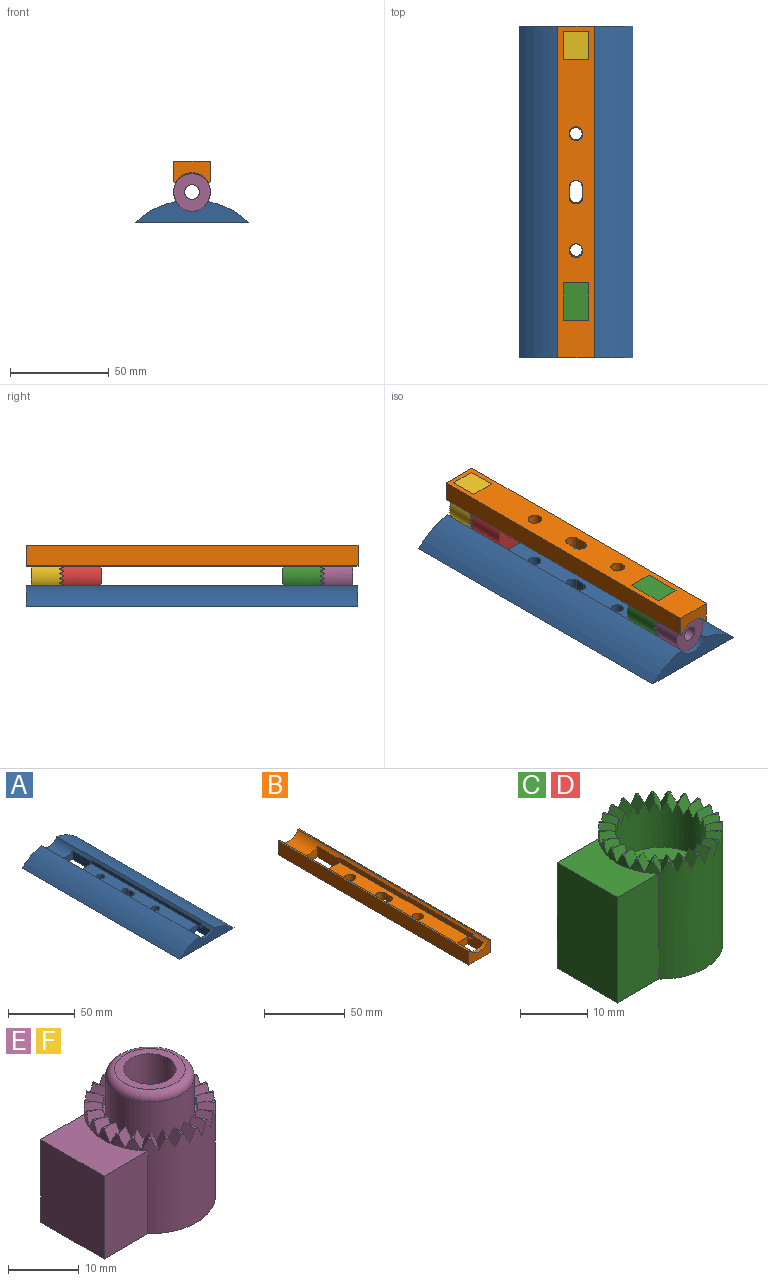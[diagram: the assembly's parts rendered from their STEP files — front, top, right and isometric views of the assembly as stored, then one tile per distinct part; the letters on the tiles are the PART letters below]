
ASSEMBLY  parts=6 mates=16
PART A: 27 faces, bbox 57.6x167.6x10.6 mm
  f0: plane 167.64x57.6mm, normal (0,0,-1), area 9109mm2, adj f5,f6,f7,f12,f13,f14,f15,f16
  f1: plane 117.05x14mm, normal (0,0,1), area 1462.5mm2, adj f3,f4,f8,f9,f10,f11,f13,f15
  f2: cylinder r=9.4mm len=167.64mm, axis (0,1,0), area 1121mm2, adj f3,f4,f5,f6,f7,f8,f9,f10
  f3: plane 3.63x0.65mm, normal (0,-1,0), area 2.1mm2, adj f1,f2,f8,f18
  f4: plane 3.63x0.65mm, normal (0,1,0), area 2.1mm2, adj f1,f2,f10,f16
  f5: cylinder r=42.03mm len=167.64mm, axis (0,1,0), area 3926.7mm2, adj f0,f2,f7,f12
  f6: cylinder r=42.03mm len=167.64mm, axis (0,1,0), area 3926.7mm2, adj f0,f2,f7,f12
  f7: plane 57.6x10.6mm, normal (0,1,0), area 385.4mm2, adj f0,f2,f5,f6
  f8: plane 117.05x3.63mm, normal (1,0,0), area 424.6mm2, adj f1,f2,f3,f11
  f9: plane 3.63x0.65mm, normal (0,-1,0), area 2.1mm2, adj f1,f2,f10,f20
  f10: plane 117.05x3.63mm, normal (-1,0,0), area 424.6mm2, adj f1,f2,f4,f9
  f11: plane 3.63x0.65mm, normal (0,1,0), area 2.1mm2, adj f1,f2,f8,f15
  f12: plane 57.6x10.6mm, normal (0,-1,0), area 385.4mm2, adj f0,f2,f5,f6
  f13: plane 12.7x5.2mm, normal (0,-1,0), area 66mm2, adj f0,f1,f15,f16
  f14: plane 12.7x8.17mm, normal (0,1,0), area 82.2mm2, adj f0,f2,f15,f16
  f15: plane 14.3x8.17mm, normal (1,0,0), area 104.1mm2, adj f0,f1,f2,f11,f13,f14
  f16: plane 14.3x8.17mm, normal (-1,0,0), area 104.1mm2, adj f0,f1,f2,f4,f13,f14
  f17: plane 12.7x5.2mm, normal (0,1,0), area 66mm2, adj f0,f1,f18,f20
  f18: plane 19.2x8.17mm, normal (1,0,0), area 156.9mm2, adj f0,f2,f3,f17,f19
  f19: plane 12.7x8.17mm, normal (0,-1,0), area 82.2mm2, adj f0,f2,f18,f20
  f20: plane 19.2x8.17mm, normal (-1,0,0), area 156.9mm2, adj f0,f2,f9,f17,f19
  f21: plane 5.2x5mm, normal (-1,0,0), area 26mm2, adj f0,f1,f22,f24
  f22: cylinder r=3.1mm len=6.2mm, axis (0,0,1), area 50.6mm2, adj f0,f1,f21,f23
  f23: plane 5.2x5mm, normal (1,0,0), area 26mm2, adj f0,f1,f22,f24
  f24: cylinder r=3.1mm len=6.2mm, axis (0,0,1), area 50.6mm2, adj f0,f1,f21,f23
  f25: cylinder r=3.1mm len=6.2mm, axis (0,0,1), area 101.3mm2, adj f0,f1
  f26: cylinder r=3.1mm len=6.2mm, axis (0,0,1), area 101.3mm2, adj f0,f1
PART B: 29 faces, bbox 18.5x167.6x10.6 mm
  f0: plane 167.64x18.5mm, normal (0,0,-1), area 2531.3mm2, adj f1,f2,f13,f14,f15,f16,f17,f18
  f1: plane 18.5x10.6mm, normal (0,1,0), area 138.4mm2, adj f0,f4,f7,f8,f27,f28
  f2: plane 18.5x10.6mm, normal (0,-1,0), area 138.4mm2, adj f0,f4,f7,f8,f27,f28
  f3: plane 117.05x14mm, normal (0,0,1), area 1439mm2, adj f5,f6,f9,f10,f11,f12,f13,f15
  f4: cylinder r=9.4mm len=167.64mm, axis (0,1,0), area 1121mm2, adj f1,f2,f5,f6,f7,f8,f9,f10
  f5: plane 3.63x0.65mm, normal (0,-1,0), area 2.1mm2, adj f3,f4,f9,f18
  f6: plane 3.63x0.65mm, normal (0,1,0), area 2.1mm2, adj f3,f4,f11,f16
  f7: cylinder r=42.03mm len=167.64mm, axis (0,1,0), area 171.4mm2, adj f1,f2,f4,f28
  f8: cylinder r=42.03mm len=167.64mm, axis (0,1,0), area 171.4mm2, adj f1,f2,f4,f27
  f9: plane 117.05x3.63mm, normal (1,0,0), area 424.6mm2, adj f3,f4,f5,f12
  f10: plane 3.63x0.65mm, normal (0,-1,0), area 2.1mm2, adj f3,f4,f11,f20
  f11: plane 117.05x3.63mm, normal (-1,0,0), area 424.6mm2, adj f3,f4,f6,f10
  f12: plane 3.63x0.65mm, normal (0,1,0), area 2.1mm2, adj f3,f4,f9,f15
  f13: plane 12.7x5.2mm, normal (0,-1,0), area 66mm2, adj f0,f3,f15,f16
  f14: plane 12.7x8.17mm, normal (0,1,0), area 82.2mm2, adj f0,f4,f15,f16
  f15: plane 14.3x8.17mm, normal (1,0,0), area 104.1mm2, adj f0,f3,f4,f12,f13,f14
  f16: plane 14.3x8.17mm, normal (-1,0,0), area 104.1mm2, adj f0,f3,f4,f6,f13,f14
  f17: plane 12.7x5.2mm, normal (0,1,0), area 66mm2, adj f0,f3,f18,f20
  f18: plane 19.2x8.17mm, normal (1,0,0), area 156.9mm2, adj f0,f4,f5,f17,f19
  f19: plane 12.7x8.17mm, normal (0,-1,0), area 82.2mm2, adj f0,f4,f18,f20
  f20: plane 19.2x8.17mm, normal (-1,0,0), area 156.9mm2, adj f0,f4,f10,f17,f19
  f21: plane 5.2x5mm, normal (-1,0,0), area 26mm2, adj f0,f3,f22,f24
  f22: cylinder r=3.43mm len=6.86mm, axis (0,0,1), area 56mm2, adj f0,f3,f21,f23
  f23: plane 5.2x5mm, normal (1,0,0), area 26mm2, adj f0,f3,f22,f24
  f24: cylinder r=3.43mm len=6.86mm, axis (0,0,1), area 56mm2, adj f0,f3,f21,f23
  f25: cylinder r=3.43mm len=6.86mm, axis (0,0,1), area 112mm2, adj f0,f3
  f26: cylinder r=3.43mm len=6.86mm, axis (0,0,1), area 112mm2, adj f0,f3
  f27: plane 167.64x10.39mm, normal (1,0,0), area 1741.3mm2, adj f0,f1,f2,f8
  f28: plane 167.64x10.39mm, normal (-1,0,0), area 1741.3mm2, adj f0,f1,f2,f7
PART C: 85 faces, bbox 24.7x18.5x21.2 mm
  f0: plane 24.7x18.5mm, normal (0,0,-1), area 314.5mm2, adj f45,f55,f56,f57,f59
  f1: plane 1.5x0.39mm, normal (0,0,1), area 0.3mm2, adj f3,f6,f83
  f2: plane 1.45x0.75mm, normal (0,0,1), area 0.3mm2, adj f4,f7,f84
  f3: cylinder r=9.25mm len=2.39mm, axis (0,0,-1), area 2.8mm2, adj f1,f6,f60,f83
  f4: cylinder r=9.25mm len=2.23mm, axis (0,0,-1), area 2.8mm2, adj f2,f7,f60,f84
  f5: cylinder r=6.75mm len=13.5mm, axis (0,0,1), area 312.6mm2, adj f6,f7,f9,f11,f13,f15,f17,f19
  f6: plane 2.56x2mm, normal (0,-0.89,0.45), area 5.5mm2, adj f1,f3,f5,f54,f83
  f7: plane 2.63x2.05mm, normal (0.45,0.77,0.45), area 5.5mm2, adj f2,f4,f5,f82,f84
  f8: plane 1.3x1.06mm, normal (0,0,1), area 0.3mm2, adj f9,f45,f82
  f9: plane 2.45x2.44mm, normal (0.63,0.63,0.45), area 5.5mm2, adj f5,f8,f45,f81,f82
  f10: plane 1.3x1.06mm, normal (0,0,1), area 0.3mm2, adj f11,f45,f81
  f11: plane 2.66x2.1mm, normal (0.77,0.45,0.45), area 5.5mm2, adj f5,f10,f45,f80,f81
  f12: plane 1.45x0.75mm, normal (0,0,1), area 0.3mm2, adj f13,f45,f80
  f13: plane 2.7x2mm, normal (0.86,0.23,0.45), area 5.5mm2, adj f5,f12,f45,f79,f80
  f14: plane 1.5x0.39mm, normal (0,0,1), area 0.3mm2, adj f15,f45,f79
  f15: plane 2.56x2mm, normal (0.89,0,0.45), area 5.5mm2, adj f5,f14,f45,f78,f79
  f16: plane 1.5x0.39mm, normal (0,0,1), area 0.3mm2, adj f17,f45,f78
  f17: plane 2.63x2mm, normal (0.86,-0.23,0.45), area 5.5mm2, adj f5,f16,f45,f77,f78
  f18: plane 1.45x0.75mm, normal (0,0,1), area 0.3mm2, adj f19,f45,f77
  f19: plane 2.63x2.05mm, normal (0.77,-0.45,0.45), area 5.5mm2, adj f5,f18,f45,f76,f77
  f20: plane 1.3x1.06mm, normal (0,0,1), area 0.3mm2, adj f21,f45,f76
  f21: plane 2.45x2.44mm, normal (0.63,-0.63,0.45), area 5.5mm2, adj f5,f20,f45,f75,f76
  f22: plane 1.3x1.06mm, normal (0,0,1), area 0.3mm2, adj f23,f45,f75
  f23: plane 2.66x2.1mm, normal (0.45,-0.77,0.45), area 5.5mm2, adj f5,f22,f45,f74,f75
  f24: plane 1.45x0.75mm, normal (0,0,1), area 0.3mm2, adj f25,f45,f74
  f25: plane 2.7x2mm, normal (0.23,-0.86,0.45), area 5.5mm2, adj f5,f24,f45,f73,f74
  f26: plane 1.5x0.39mm, normal (0,0,1), area 0.3mm2, adj f27,f45,f73
  f27: plane 2.56x2mm, normal (0,-0.89,0.45), area 5.5mm2, adj f5,f26,f45,f72,f73
  f28: plane 1.5x0.39mm, normal (0,0,1), area 0.3mm2, adj f29,f45,f72
  f29: plane 2.63x2mm, normal (-0.23,-0.86,0.45), area 5.5mm2, adj f5,f28,f45,f71,f72
  f30: plane 1.45x0.75mm, normal (0,0,1), area 0.3mm2, adj f31,f45,f71
  f31: plane 2.63x2.05mm, normal (-0.45,-0.77,0.45), area 5.5mm2, adj f5,f30,f45,f70,f71
  f32: plane 1.3x1.06mm, normal (0,0,1), area 0.3mm2, adj f33,f45,f70
  f33: plane 2.45x2.44mm, normal (-0.63,-0.63,0.45), area 5.5mm2, adj f5,f32,f45,f69,f70
  f34: plane 1.3x1.06mm, normal (0,0,1), area 0.3mm2, adj f35,f45,f69
  f35: plane 2.66x2.1mm, normal (-0.77,-0.45,0.45), area 5.5mm2, adj f5,f34,f45,f68,f69
  f36: plane 1.45x0.75mm, normal (0,0,1), area 0.3mm2, adj f37,f45,f68
  f37: plane 2.7x2mm, normal (-0.86,-0.23,0.45), area 5.5mm2, adj f5,f36,f45,f67,f68
  f38: plane 1.5x0.39mm, normal (0,0,1), area 0.3mm2, adj f39,f45,f67
  f39: plane 2.56x2mm, normal (-0.89,0,0.45), area 5.5mm2, adj f5,f38,f45,f66,f67
  f40: plane 1.5x0.39mm, normal (0,0,1), area 0.3mm2, adj f41,f45,f66
  f41: plane 2.63x2mm, normal (-0.86,0.23,0.45), area 5.5mm2, adj f5,f40,f45,f65,f66
  f42: plane 1.45x0.75mm, normal (0,0,1), area 0.3mm2, adj f43,f45,f65
  f43: plane 2.63x2.05mm, normal (-0.77,0.45,0.45), area 5.5mm2, adj f5,f42,f45,f64,f65
  f44: plane 1.3x1.06mm, normal (0,0,1), area 0.3mm2, adj f45,f46,f64
  f45: cylinder r=9.25mm len=21.2mm, axis (0,0,-1), area 903.4mm2, adj f0,f8,f9,f10,f11,f12,f13,f14
  f46: plane 2.45x2.44mm, normal (-0.63,0.63,0.45), area 5.5mm2, adj f5,f44,f45,f63,f64
  f47: plane 1.3x1.06mm, normal (0,0,1), area 0.3mm2, adj f45,f48,f63
  f48: plane 2.66x2.1mm, normal (-0.45,0.77,0.45), area 5.5mm2, adj f5,f45,f47,f62,f63
  f49: plane 1.45x0.75mm, normal (0,0,1), area 0.3mm2, adj f50,f51,f62
  f50: cylinder r=9.25mm len=2.23mm, axis (0,0,-1), area 2.8mm2, adj f49,f51,f60,f62
  f51: plane 2.7x2mm, normal (-0.23,0.86,0.45), area 5.5mm2, adj f5,f49,f50,f61,f62
  f52: plane 1.5x0.39mm, normal (0,0,1), area 0.3mm2, adj f53,f54,f61
  f53: cylinder r=9.25mm len=2.39mm, axis (0,0,-1), area 2.8mm2, adj f52,f54,f60,f61
  f54: plane 2.56x2mm, normal (0,0.89,0.45), area 5.5mm2, adj f5,f6,f52,f53,f61
  f55: plane 19.2x8.72mm, normal (0,1,0), area 167.5mm2, adj f0,f45,f56,f60
  f56: plane 19.2x12.7mm, normal (-1,0,0), area 243.8mm2, adj f0,f55,f57,f60
  f57: plane 19.2x8.72mm, normal (0,-1,0), area 167.5mm2, adj f0,f45,f56,f60
  f58: plane 13.5x13.5mm, normal (0,0,1), area 100.1mm2, adj f5,f59
  f59: cylinder r=3.7mm len=12.7mm, axis (0,0,1), area 295.4mm2, adj f0,f58
  f60: plane 12.7x8.72mm, normal (0,0,1), area 88.8mm2, adj f3,f4,f45,f50,f53,f55,f56,f57
  f61: plane 2.63x2mm, normal (0.23,-0.86,0.45), area 5.5mm2, adj f5,f51,f52,f53,f54
  f62: plane 2.63x2.05mm, normal (0.45,-0.77,0.45), area 5.5mm2, adj f5,f48,f49,f50,f51
  f63: plane 2.45x2.44mm, normal (0.63,-0.63,0.45), area 5.5mm2, adj f5,f45,f46,f47,f48
  f64: plane 2.66x2.1mm, normal (0.77,-0.45,0.45), area 5.5mm2, adj f5,f43,f44,f45,f46
  f65: plane 2.7x2mm, normal (0.86,-0.23,0.45), area 5.5mm2, adj f5,f41,f42,f43,f45
  f66: plane 2.56x2mm, normal (0.89,0,0.45), area 5.5mm2, adj f5,f39,f40,f41,f45
  f67: plane 2.63x2mm, normal (0.86,0.23,0.45), area 5.5mm2, adj f5,f37,f38,f39,f45
  f68: plane 2.63x2.05mm, normal (0.77,0.45,0.45), area 5.5mm2, adj f5,f35,f36,f37,f45
  f69: plane 2.45x2.44mm, normal (0.63,0.63,0.45), area 5.5mm2, adj f5,f33,f34,f35,f45
  f70: plane 2.66x2.1mm, normal (0.45,0.77,0.45), area 5.5mm2, adj f5,f31,f32,f33,f45
  f71: plane 2.7x2mm, normal (0.23,0.86,0.45), area 5.5mm2, adj f5,f29,f30,f31,f45
  f72: plane 2.56x2mm, normal (0,0.89,0.45), area 5.5mm2, adj f5,f27,f28,f29,f45
  f73: plane 2.63x2mm, normal (-0.23,0.86,0.45), area 5.5mm2, adj f5,f25,f26,f27,f45
  f74: plane 2.63x2.05mm, normal (-0.45,0.77,0.45), area 5.5mm2, adj f5,f23,f24,f25,f45
  f75: plane 2.45x2.44mm, normal (-0.63,0.63,0.45), area 5.5mm2, adj f5,f21,f22,f23,f45
  f76: plane 2.66x2.1mm, normal (-0.77,0.45,0.45), area 5.5mm2, adj f5,f19,f20,f21,f45
  f77: plane 2.7x2mm, normal (-0.86,0.23,0.45), area 5.5mm2, adj f5,f17,f18,f19,f45
  f78: plane 2.56x2mm, normal (-0.89,0,0.45), area 5.5mm2, adj f5,f15,f16,f17,f45
  f79: plane 2.63x2mm, normal (-0.86,-0.23,0.45), area 5.5mm2, adj f5,f13,f14,f15,f45
  f80: plane 2.63x2.05mm, normal (-0.77,-0.45,0.45), area 5.5mm2, adj f5,f11,f12,f13,f45
  f81: plane 2.45x2.44mm, normal (-0.63,-0.63,0.45), area 5.5mm2, adj f5,f9,f10,f11,f45
  f82: plane 2.66x2.1mm, normal (-0.45,-0.77,0.45), area 5.5mm2, adj f5,f7,f8,f9,f45
  f83: plane 2.63x2mm, normal (0.23,0.86,0.45), area 5.5mm2, adj f1,f3,f5,f6,f84
  f84: plane 2.7x2mm, normal (-0.23,-0.86,0.45), area 5.5mm2, adj f2,f4,f5,f7,f83
PART D: same geometry as C
PART E: 112 faces, bbox 24.7x18.5x21.9 mm
  f0: plane 24.7x18.5mm, normal (0,0,-1), area 314.5mm2, adj f68,f79,f80,f81,f82
  f1: cylinder r=6.75mm len=1.74mm, axis (0,0,1), area 1.5mm2, adj f48,f97,f108
  f2: cylinder r=6.75mm len=1.74mm, axis (0,0,1), area 1.5mm2, adj f46,f98,f108
  f3: cylinder r=6.75mm len=1.74mm, axis (0,0,1), area 1.5mm2, adj f44,f99,f108
  f4: cylinder r=6.75mm len=1.74mm, axis (0,0,1), area 1.5mm2, adj f42,f100,f108
  f5: cylinder r=6.75mm len=1.74mm, axis (0,0,1), area 1.5mm2, adj f40,f101,f108
  f6: cylinder r=6.75mm len=1.76mm, axis (0,0,1), area 1.5mm2, adj f38,f102,f108
  f7: cylinder r=6.75mm len=1.74mm, axis (0,0,1), area 1.5mm2, adj f36,f103,f108
  f8: cylinder r=6.75mm len=1.74mm, axis (0,0,1), area 1.5mm2, adj f34,f104,f108
  f9: cylinder r=6.75mm len=1.74mm, axis (0,0,1), area 1.5mm2, adj f32,f105,f108
  f10: cylinder r=6.75mm len=1.74mm, axis (0,0,1), area 1.5mm2, adj f30,f107,f108
  f11: cylinder r=6.75mm len=1.74mm, axis (0,0,1), area 1.5mm2, adj f29,f106,f108
  f12: cylinder r=6.75mm len=1.76mm, axis (0,0,1), area 1.5mm2, adj f78,f84,f108
  f13: cylinder r=6.75mm len=1.74mm, axis (0,0,1), area 1.5mm2, adj f75,f85,f108
  f14: cylinder r=6.75mm len=1.74mm, axis (0,0,1), area 1.5mm2, adj f72,f86,f108
  f15: cylinder r=6.75mm len=1.74mm, axis (0,0,1), area 1.5mm2, adj f69,f87,f108
  f16: cylinder r=6.75mm len=1.74mm, axis (0,0,1), area 1.5mm2, adj f66,f88,f108
  f17: cylinder r=6.75mm len=1.74mm, axis (0,0,1), area 1.5mm2, adj f64,f89,f108
  f18: cylinder r=6.75mm len=1.76mm, axis (0,0,1), area 1.5mm2, adj f62,f90,f108
  f19: cylinder r=6.75mm len=1.74mm, axis (0,0,1), area 1.5mm2, adj f60,f91,f108
  f20: cylinder r=6.75mm len=1.74mm, axis (0,0,1), area 1.5mm2, adj f58,f92,f108
  f21: cylinder r=6.75mm len=1.74mm, axis (0,0,1), area 1.5mm2, adj f56,f93,f108
  f22: cylinder r=6.75mm len=1.74mm, axis (0,0,1), area 1.5mm2, adj f54,f94,f108
  f23: cylinder r=6.75mm len=1.74mm, axis (0,0,1), area 1.5mm2, adj f52,f95,f108
  f24: cylinder r=6.75mm len=1.76mm, axis (0,0,1), area 1.5mm2, adj f50,f96,f108
  f25: plane 1.49x0.57mm, normal (0,0,1), area 0.3mm2, adj f27,f29,f106
  f26: plane 1.39x0.91mm, normal (0,0,1), area 0.3mm2, adj f28,f30,f107
  f27: cylinder r=9.25mm len=2.33mm, axis (0,0,-1), area 2.8mm2, adj f25,f29,f83,f106
  f28: cylinder r=9.25mm len=2.09mm, axis (0,0,-1), area 2.8mm2, adj f26,f30,f83,f107
  f29: plane 2.65x2mm, normal (-0.12,-0.88,0.45), area 5.5mm2, adj f11,f25,f27,f78,f106
  f30: plane 2.56x2.26mm, normal (0.54,0.71,0.45), area 5.5mm2, adj f10,f26,f28,f105,f107
  f31: plane 1.19x1.19mm, normal (0,0,1), area 0.3mm2, adj f32,f68,f105
  f32: plane 2.57x2.3mm, normal (0.71,0.54,0.45), area 5.5mm2, adj f9,f31,f68,f104,f105
  f33: plane 1.39x0.91mm, normal (0,0,1), area 0.3mm2, adj f34,f68,f104
  f34: plane 2.7x2mm, normal (0.82,0.34,0.45), area 5.5mm2, adj f8,f33,f68,f103,f104
  f35: plane 1.49x0.57mm, normal (0,0,1), area 0.3mm2, adj f36,f68,f103
  f36: plane 2.65x2mm, normal (0.88,0.12,0.45), area 5.5mm2, adj f7,f35,f68,f102,f103
  f37: plane 1.49x0.39mm, normal (0,0,1), area 0.3mm2, adj f38,f68,f102
  f38: plane 2.56x2mm, normal (0.88,-0.12,0.45), area 5.5mm2, adj f6,f37,f68,f101,f102
  f39: plane 1.49x0.57mm, normal (0,0,1), area 0.3mm2, adj f40,f68,f101
  f40: plane 2.65x2mm, normal (0.82,-0.34,0.45), area 5.5mm2, adj f5,f39,f68,f100,f101
  f41: plane 1.39x0.91mm, normal (0,0,1), area 0.3mm2, adj f42,f68,f100
  f42: plane 2.56x2.26mm, normal (0.71,-0.54,0.45), area 5.5mm2, adj f4,f41,f68,f99,f100
  f43: plane 1.19x1.19mm, normal (0,0,1), area 0.3mm2, adj f44,f68,f99
  f44: plane 2.57x2.3mm, normal (0.54,-0.71,0.45), area 5.5mm2, adj f3,f43,f68,f98,f99
  f45: plane 1.39x0.91mm, normal (0,0,1), area 0.3mm2, adj f46,f68,f98
  f46: plane 2.7x2mm, normal (0.34,-0.82,0.45), area 5.5mm2, adj f2,f45,f68,f97,f98
  f47: plane 1.49x0.57mm, normal (0,0,1), area 0.3mm2, adj f48,f68,f97
  f48: plane 2.65x2mm, normal (0.12,-0.88,0.45), area 5.5mm2, adj f1,f47,f68,f96,f97
  f49: plane 1.49x0.39mm, normal (0,0,1), area 0.3mm2, adj f50,f68,f96
  f50: plane 2.56x2mm, normal (-0.12,-0.88,0.45), area 5.5mm2, adj f24,f49,f68,f95,f96
  f51: plane 1.49x0.57mm, normal (0,0,1), area 0.3mm2, adj f52,f68,f95
  f52: plane 2.65x2mm, normal (-0.34,-0.82,0.45), area 5.5mm2, adj f23,f51,f68,f94,f95
  f53: plane 1.39x0.91mm, normal (0,0,1), area 0.3mm2, adj f54,f68,f94
  f54: plane 2.56x2.26mm, normal (-0.54,-0.71,0.45), area 5.5mm2, adj f22,f53,f68,f93,f94
  f55: plane 1.19x1.19mm, normal (0,0,1), area 0.3mm2, adj f56,f68,f93
  f56: plane 2.57x2.3mm, normal (-0.71,-0.54,0.45), area 5.5mm2, adj f21,f55,f68,f92,f93
  f57: plane 1.39x0.91mm, normal (0,0,1), area 0.3mm2, adj f58,f68,f92
  f58: plane 2.7x2mm, normal (-0.82,-0.34,0.45), area 5.5mm2, adj f20,f57,f68,f91,f92
  f59: plane 1.49x0.57mm, normal (0,0,1), area 0.3mm2, adj f60,f68,f91
  f60: plane 2.65x2mm, normal (-0.88,-0.12,0.45), area 5.5mm2, adj f19,f59,f68,f90,f91
  f61: plane 1.49x0.39mm, normal (0,0,1), area 0.3mm2, adj f62,f68,f90
  f62: plane 2.56x2mm, normal (-0.88,0.12,0.45), area 5.5mm2, adj f18,f61,f68,f89,f90
  f63: plane 1.49x0.57mm, normal (0,0,1), area 0.3mm2, adj f64,f68,f89
  f64: plane 2.65x2mm, normal (-0.82,0.34,0.45), area 5.5mm2, adj f17,f63,f68,f88,f89
  f65: plane 1.39x0.91mm, normal (0,0,1), area 0.3mm2, adj f66,f68,f88
  f66: plane 2.56x2.26mm, normal (-0.71,0.54,0.45), area 5.5mm2, adj f16,f65,f68,f87,f88
  f67: plane 1.19x1.19mm, normal (0,0,1), area 0.3mm2, adj f68,f69,f87
  f68: cylinder r=9.25mm len=18.5mm, axis (0,0,-1), area 684.4mm2, adj f0,f31,f32,f33,f34,f35,f36,f37
  f69: plane 2.57x2.3mm, normal (-0.54,0.71,0.45), area 5.5mm2, adj f15,f67,f68,f86,f87
  f70: plane 1.39x0.91mm, normal (0,0,1), area 0.3mm2, adj f71,f72,f86
  f71: cylinder r=9.25mm len=2.09mm, axis (0,0,-1), area 2.8mm2, adj f70,f72,f83,f86
  f72: plane 2.7x2mm, normal (-0.34,0.82,0.45), area 5.5mm2, adj f14,f70,f71,f85,f86
  f73: plane 1.49x0.57mm, normal (0,0,1), area 0.3mm2, adj f74,f75,f85
  f74: cylinder r=9.25mm len=2.33mm, axis (0,0,-1), area 2.8mm2, adj f73,f75,f83,f85
  f75: plane 2.65x2mm, normal (-0.12,0.88,0.45), area 5.5mm2, adj f13,f73,f74,f84,f85
  f76: plane 1.49x0.39mm, normal (0,0,1), area 0.3mm2, adj f77,f78,f84
  f77: cylinder r=9.25mm len=2.41mm, axis (0,0,-1), area 2.8mm2, adj f76,f78,f83,f84
  f78: plane 2.56x2mm, normal (0.12,0.88,0.45), area 5.5mm2, adj f12,f29,f76,f77,f84
  f79: plane 14.3x8.72mm, normal (0,1,0), area 124.8mm2, adj f0,f68,f80,f83
  f80: plane 14.3x12.7mm, normal (-1,0,0), area 181.6mm2, adj f0,f79,f81,f83
  f81: plane 14.3x8.72mm, normal (0,-1,0), area 124.8mm2, adj f0,f68,f80,f83
  f82: cylinder r=3.7mm len=21.92mm, axis (0,0,1), area 509.9mm2, adj f0,f110
  f83: plane 12.7x8.72mm, normal (0,0,1), area 88.8mm2, adj f27,f28,f68,f71,f74,f77,f79,f80
  f84: plane 2.56x2mm, normal (0.12,-0.88,0.45), area 5.5mm2, adj f12,f75,f76,f77,f78
  f85: plane 2.65x2mm, normal (0.34,-0.82,0.45), area 5.5mm2, adj f13,f72,f73,f74,f75
  f86: plane 2.56x2.26mm, normal (0.54,-0.71,0.45), area 5.5mm2, adj f14,f69,f70,f71,f72
  f87: plane 2.57x2.3mm, normal (0.71,-0.54,0.45), area 5.5mm2, adj f15,f66,f67,f68,f69
  f88: plane 2.7x2mm, normal (0.82,-0.34,0.45), area 5.5mm2, adj f16,f64,f65,f66,f68
  f89: plane 2.65x2mm, normal (0.88,-0.12,0.45), area 5.5mm2, adj f17,f62,f63,f64,f68
  f90: plane 2.56x2mm, normal (0.88,0.12,0.45), area 5.5mm2, adj f18,f60,f61,f62,f68
  f91: plane 2.65x2mm, normal (0.82,0.34,0.45), area 5.5mm2, adj f19,f58,f59,f60,f68
  f92: plane 2.56x2.26mm, normal (0.71,0.54,0.45), area 5.5mm2, adj f20,f56,f57,f58,f68
  f93: plane 2.57x2.3mm, normal (0.54,0.71,0.45), area 5.5mm2, adj f21,f54,f55,f56,f68
  f94: plane 2.7x2mm, normal (0.34,0.82,0.45), area 5.5mm2, adj f22,f52,f53,f54,f68
  f95: plane 2.65x2mm, normal (0.12,0.88,0.45), area 5.5mm2, adj f23,f50,f51,f52,f68
  f96: plane 2.56x2mm, normal (-0.12,0.88,0.45), area 5.5mm2, adj f24,f48,f49,f50,f68
  f97: plane 2.65x2mm, normal (-0.34,0.82,0.45), area 5.5mm2, adj f1,f46,f47,f48,f68
  f98: plane 2.56x2.26mm, normal (-0.54,0.71,0.45), area 5.5mm2, adj f2,f44,f45,f46,f68
  f99: plane 2.57x2.3mm, normal (-0.71,0.54,0.45), area 5.5mm2, adj f3,f42,f43,f44,f68
  f100: plane 2.7x2mm, normal (-0.82,0.34,0.45), area 5.5mm2, adj f4,f40,f41,f42,f68
  f101: plane 2.65x2mm, normal (-0.88,0.12,0.45), area 5.5mm2, adj f5,f38,f39,f40,f68
  f102: plane 2.56x2mm, normal (-0.88,-0.12,0.45), area 5.5mm2, adj f6,f36,f37,f38,f68
  f103: plane 2.65x2mm, normal (-0.82,-0.34,0.45), area 5.5mm2, adj f7,f34,f35,f36,f68
  f104: plane 2.56x2.26mm, normal (-0.71,-0.54,0.45), area 5.5mm2, adj f8,f32,f33,f34,f68
  f105: plane 2.57x2.3mm, normal (-0.54,-0.71,0.45), area 5.5mm2, adj f9,f30,f31,f32,f68
  f106: plane 2.65x2mm, normal (0.34,0.82,0.45), area 5.5mm2, adj f11,f25,f27,f29,f107
  f107: plane 2.7x2mm, normal (-0.34,-0.82,0.45), area 5.5mm2, adj f10,f26,f28,f30,f106
  f108: plane 13.5x13.5mm, normal (0,0,1), area 20.4mm2, adj f1,f2,f3,f4,f5,f6,f7,f8
  f109: cylinder r=6.25mm len=12.5mm, axis (0,0,-1), area 249.4mm2, adj f108,f111
  f110: plane 9.96x9.96mm, normal (0,0,1), area 34.9mm2, adj f82,f111
  f111: torus R=4.98mm, axis (0,0,1), area 72.6mm2, adj f109,f110
PART F: same geometry as E
PLACE A t=(-28.8,83.82,0)mm
PLACE B rot(axis=(1,0,0),180deg) t=(-28.8,-83.99,30.9)mm
PLACE C rot(axis=(0.58,0.58,-0.58),120deg) t=(-9.25,-45.94,30.9)mm
PLACE D rot(axis=(-0.58,-0.58,-0.58),120deg) t=(-9.25,45.78,0)mm
PLACE E rot(axis=(-0.58,-0.58,-0.58),120deg) t=(-9.25,-81.28,0)mm
PLACE F rot(axis=(0.58,0.58,-0.58),120deg) t=(-9.25,81.11,30.9)mm
MATE planar E.f80 <-> D.f56  axis (0,0,-1) through (0,-74.13,0)mm
MATE planar E.f79 <-> A.f16  axis (1,0,0) through (6.35,-81.28,8.72)mm
MATE planar D.f0 <-> A.f3  axis (0,-1,0) through (0,45.78,12.09)mm
MATE parallel E.f80 <-> A.f0  axis (0,0,-1) through (0,-74.13,0)mm
MATE planar E.f79 <-> D.f55  axis (1,0,0) through (6.35,-74.13,4.36)mm
MATE planar F.f81 <-> B.f15  axis (-1,0,0) through (-6.35,73.96,26.54)mm
MATE planar C.f60 <-> B.f19  axis (0,-1,0) through (0,-65.14,27.37)mm
MATE cylindrical F.f1 <-> D.f3  axis (0,1,0) through (0,63.64,15.45)mm
MATE planar F.f80 <-> B.f0  axis (0,0,1) through (0,73.96,30.9)mm
MATE planar C.f57 <-> B.f18  axis (-1,0,0) through (-6.35,-55.54,26.54)mm
MATE planar E.f80 <-> A.f0  axis (0,0,-1) through (0,-74.13,0)mm
MATE cylindrical B.f25 <-> A.f26  axis (0,0,-1) through (0,29.4,28.3)mm
MATE planar C.f56 <-> B.f0  axis (0,0,1) through (0,-55.54,30.9)mm
MATE parallel D.f0 <-> E.f0  axis (0,-1,0) through (0,45.78,12.09)mm
MATE planar B.f13 <-> F.f83  axis (0,1,0) through (0,66.81,28.3)mm
MATE planar E.f0 <-> A.f14  axis (0,-1,0) through (0,-81.28,0)mm
